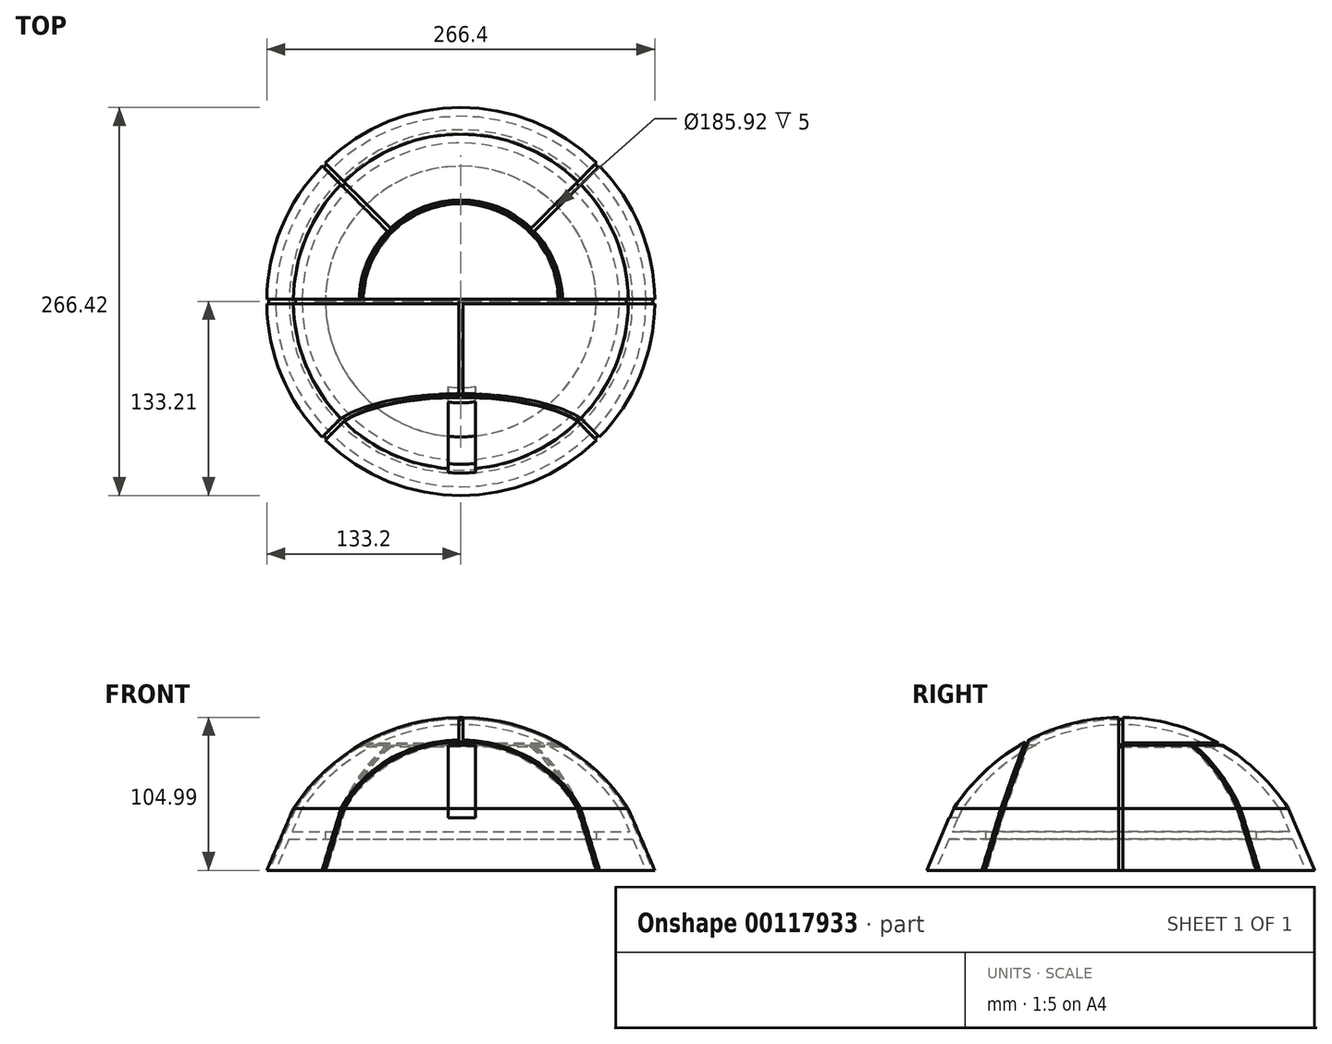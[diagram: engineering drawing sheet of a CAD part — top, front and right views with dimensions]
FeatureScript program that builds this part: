
annotation { "Feature Type Name" : "Feature", "Feature Type Description" : "" }
export const myFeature = defineFeature(function(context is Context, id is Id, definition is map)
    precondition{}
    {
        {
            var Q0;
            Q0=qCreatedBy(makeId("Front.planeOp"),FACE);
            var sketch = newSketch(context, id + "F0", { "sketchPlane" : qUnion([Q0])});
            skArc(sketch, "E0", {"start": v(114.97, 74.5) * mm, "mid": v(0, 137) * mm, "end": v(-114.97, 74.5) * mm});
            skLineSegment(sketch, "E1", {"start": v(-137, 0) * mm, "end": v(137, 0) * mm});
            skLineSegment(sketch, "E2", {"start": v(-133.21, 32) * mm, "end": v(133.21, 32) * mm});
            skLineSegment(sketch, "E3", {"start": v(-114.97, 74.5) * mm, "end": v(114.97, 74.5) * mm});
            skLineSegment(sketch, "E4", {"start": v(-114.97, 74.5) * mm, "end": v(-133.21, 32) * mm});
            skLineSegment(sketch, "E5", {"start": v(114.97, 74.5) * mm, "end": v(133.21, 32) * mm});
            skLineSegment(sketch, "E6", {"start": v(0, 137) * mm, "end": v(-99.44, 137) * mm, "construction": true});
            skLineSegment(sketch, "E7", {"start": v(0, 0) * mm, "end": v(0, 137) * mm});
            skArc(sketch, "E8", {"start": v(128.06, 32) * mm, "mid": v(0, 132) * mm, "end": v(-128.06, 32) * mm});
            skLineSegment(sketch, "E9", {"start": v(-108.97, 74.5) * mm, "end": v(-127.2, 32) * mm});
            skLineSegment(sketch, "E10", {"start": v(-115.81, 58.54) * mm, "end": v(-92.96, 58.54) * mm});
            skLineSegment(sketch, "E11", {"start": v(-92.96, 58.54) * mm, "end": v(-92.96, 53.54) * mm});
            skLineSegment(sketch, "E12", {"start": v(-92.96, 53.54) * mm, "end": v(-117.96, 53.54) * mm});
            skLineSegment(sketch, "E13", {"start": v(108.97, 74.5) * mm, "end": v(128.06, 32) * mm});
            skSolve(sketch);
        }
        {
            var Q0;
            {var subQ0=sQuery(id+"F0.wireOp",EDGE,"E4");Q0=makeQuery(id+"F0.imprint","IMPRINT",FACE,{"disambiguationData":[TD([[makeQuery(id+"F0.imprint","IMPRINT",EDGE,{"derivedFrom":subQ0}),1.0]])]});}
            var Q1;
            {var subQ0=sQuery(id+"F0.wireOp",EDGE,"E9");var subQ5=sQuery(id+"F0.wireOp",EDGE,"E2");var subQ7=makeQuery(id+"F0.imprint","INTERSECT",VERTEX,{"derivedFrom":[subQ5,subQ0]});Q1=makeQuery(id+"F0.imprint","IMPRINT",FACE,{"disambiguationData":[TD([[makeQuery(id+"F0.imprint","IMPRINT",EDGE,{"disambiguationData":[TD([[subQ7,1.0]])],"derivedFrom":subQ5}),1.0]])]});}
            var Q2;
            {var subQ0=sQuery(id+"F0.wireOp",EDGE,"E10");Q2=makeQuery(id+"F0.imprint","IMPRINT",FACE,{"disambiguationData":[TD([[makeQuery(id+"F0.imprint","IMPRINT",EDGE,{"derivedFrom":subQ0}),-1.0]])]});}
            var Q3;
            {var subQ1=sQuery(id+"F0.wireOp",EDGE,"E0");var subQ3=sQuery(id+"F0.wireOp",EDGE,"E7");var subQ4=makeQuery(id+"F0.imprint","INTERSECT",VERTEX,{"derivedFrom":[subQ1,subQ3]});Q3=makeQuery(id+"F0.imprint","IMPRINT",FACE,{"disambiguationData":[TD([[makeQuery(id+"F0.imprint","IMPRINT",EDGE,{"disambiguationData":[TD([[subQ4,1.0]])],"derivedFrom":subQ3}),1.0]])]});}
            var Q4;
            Q4=sQuery(id+"F0.wireOp",EDGE,"E7");
            revolve(context, id + "F1", {"entities" : qUnion([Q0, Q1, Q2, Q3]), "axis" : qUnion([Q4]), "revolveType" : RevolveType.FULL});
        }
        {
            var Q0;
            Q0=qCreatedBy(makeId("Top.planeOp"),FACE);
            cPlane(context, id + "F2", {"entities" : qUnion([Q0]), "cplaneType" : CPlaneType.OFFSET, "offset" : 74.5 * mm, "width" : 150 * mm, "height" : 150 * mm});
        }
        {
            var Q0;
            Q0=qCreatedBy(id+"F2.planeOp",FACE);
            var sketch = newSketch(context, id + "F3", { "sketchPlane" : qUnion([Q0])});
            skLineSegment(sketch, "E14", {"start": v(0, 0) * mm, "end": v(-58.68, 0) * mm, "construction": true});
            skLineSegment(sketch, "E15.bottom", {"start": v(-113.47, 1.5) * mm, "end": v(-116.47, 1.5) * mm});
            skLineSegment(sketch, "E15.top", {"start": v(-113.47, -1.5) * mm, "end": v(-116.47, -1.5) * mm});
            skLineSegment(sketch, "E15.left", {"start": v(-113.47, 1.5) * mm, "end": v(-113.47, -1.5) * mm});
            skLineSegment(sketch, "E15.right", {"start": v(-116.47, 1.5) * mm, "end": v(-116.47, -1.5) * mm});
            skPoint(sketch, "E15.middle", {"position": v(-114.97, 0) * mm});
            skLineSegment(sketch, "E16.1.0", {"start": v(-81.3, -79.18) * mm, "end": v(-83.42, -81.3) * mm});
            skLineSegment(sketch, "E16.1.1", {"start": v(-81.3, -79.18) * mm, "end": v(-79.18, -81.3) * mm});
            skLineSegment(sketch, "E16.1.2", {"start": v(-79.18, -81.3) * mm, "end": v(-81.3, -83.42) * mm});
            skLineSegment(sketch, "E16.1.3", {"start": v(-83.42, -81.3) * mm, "end": v(-81.3, -83.42) * mm});
            skLineSegment(sketch, "E16.2.0", {"start": v(-1.5, -113.47) * mm, "end": v(-1.5, -116.47) * mm});
            skLineSegment(sketch, "E16.2.1", {"start": v(-1.5, -113.47) * mm, "end": v(1.5, -113.47) * mm});
            skLineSegment(sketch, "E16.2.2", {"start": v(1.5, -113.47) * mm, "end": v(1.5, -116.47) * mm});
            skLineSegment(sketch, "E16.2.3", {"start": v(-1.5, -116.47) * mm, "end": v(1.5, -116.47) * mm});
            skLineSegment(sketch, "E16.3.0", {"start": v(79.18, -81.3) * mm, "end": v(81.3, -83.42) * mm});
            skLineSegment(sketch, "E16.3.1", {"start": v(79.18, -81.3) * mm, "end": v(81.3, -79.18) * mm});
            skLineSegment(sketch, "E16.3.2", {"start": v(81.3, -79.18) * mm, "end": v(83.42, -81.3) * mm});
            skLineSegment(sketch, "E16.3.3", {"start": v(81.3, -83.42) * mm, "end": v(83.42, -81.3) * mm});
            skLineSegment(sketch, "E16.4.0", {"start": v(113.47, -1.5) * mm, "end": v(116.47, -1.5) * mm});
            skLineSegment(sketch, "E16.4.1", {"start": v(113.47, -1.5) * mm, "end": v(113.47, 1.5) * mm});
            skLineSegment(sketch, "E16.4.2", {"start": v(113.47, 1.5) * mm, "end": v(116.47, 1.5) * mm});
            skLineSegment(sketch, "E16.4.3", {"start": v(116.47, -1.5) * mm, "end": v(116.47, 1.5) * mm});
            skLineSegment(sketch, "E16.5.0", {"start": v(81.3, 79.18) * mm, "end": v(83.42, 81.3) * mm});
            skLineSegment(sketch, "E16.5.1", {"start": v(81.3, 79.18) * mm, "end": v(79.18, 81.3) * mm});
            skLineSegment(sketch, "E16.5.2", {"start": v(79.18, 81.3) * mm, "end": v(81.3, 83.42) * mm});
            skLineSegment(sketch, "E16.5.3", {"start": v(83.42, 81.3) * mm, "end": v(81.3, 83.42) * mm});
            skLineSegment(sketch, "E16.6.0", {"start": v(1.5, 113.47) * mm, "end": v(1.5, 116.47) * mm});
            skLineSegment(sketch, "E16.6.1", {"start": v(1.5, 113.47) * mm, "end": v(-1.5, 113.47) * mm});
            skLineSegment(sketch, "E16.6.2", {"start": v(-1.5, 113.47) * mm, "end": v(-1.5, 116.47) * mm});
            skLineSegment(sketch, "E16.6.3", {"start": v(1.5, 116.47) * mm, "end": v(-1.5, 116.47) * mm});
            skLineSegment(sketch, "E16.7.0", {"start": v(-79.18, 81.3) * mm, "end": v(-81.3, 83.42) * mm});
            skLineSegment(sketch, "E16.7.1", {"start": v(-79.18, 81.3) * mm, "end": v(-81.3, 79.18) * mm});
            skLineSegment(sketch, "E16.7.2", {"start": v(-81.3, 79.18) * mm, "end": v(-83.42, 81.3) * mm});
            skLineSegment(sketch, "E16.7.3", {"start": v(-81.3, 83.42) * mm, "end": v(-83.42, 81.3) * mm});
            skPoint(sketch, "E16.center", {"position": v(0, 0) * mm});
            skLineSegment(sketch, "E17", {"start": v(81.3, -81.3) * mm, "end": v(-81.3, 81.3) * mm, "construction": true});
            skLineSegment(sketch, "E18", {"start": v(81.3, 81.3) * mm, "end": v(-81.3, -81.3) * mm, "construction": true});
            skLineSegment(sketch, "E19", {"start": v(-81.3, -81.3) * mm, "end": v(81.3, -81.3) * mm, "construction": true});
            skSolve(sketch);
        }
        {
            var Q0;
            Q0=makeQuery(id+"F3.imprint","IMPRINT",FACE,{"disambiguationData":[TD([[makeQuery(id+"F3.imprint","IMPRINT",EDGE,{"derivedFrom":sQuery(id+"F3.wireOp",EDGE,"E15.bottom")}),1.0]])]});
            var Q1;
            Q1=sQuery(id+"F0.wireOp",EDGE,"E4");
            sweep(context, id + "F4", {"operationType" : NewBodyOperationType.REMOVE, "profiles" : qUnion([Q0]), "path" : qUnion([Q1])});
        }
        {
            var Q0;
            Q0=makeQuery(id+"F3.imprint","IMPRINT",FACE,{"disambiguationData":[TD([[makeQuery(id+"F3.imprint","IMPRINT",EDGE,{"derivedFrom":sQuery(id+"F3.wireOp",EDGE,"E15.bottom")}),1.0]])]});
            var Q1;
            Q1=sQuery(id+"F0.wireOp",EDGE,"E0");
            sweep(context, id + "F5", {"operationType" : NewBodyOperationType.REMOVE, "profiles" : qUnion([Q0]), "path" : qUnion([Q1])});
        }
        {
            var Q0;
            Q0=makeQuery(id+"F3.imprint","IMPRINT",FACE,{"disambiguationData":[TD([[makeQuery(id+"F3.imprint","IMPRINT",EDGE,{"derivedFrom":sQuery(id+"F3.wireOp",EDGE,"E16.4.0")}),1.0]])]});
            var Q1;
            Q1=sQuery(id+"F0.wireOp",EDGE,"E5");
            sweep(context, id + "F6", {"operationType" : NewBodyOperationType.REMOVE, "profiles" : qUnion([Q0]), "path" : qUnion([Q1])});
        }
        {
            var Q0;
            Q0=qCreatedBy(makeId("Right.planeOp"),FACE);
            var sketch = newSketch(context, id + "F7", { "sketchPlane" : qUnion([Q0])});
            skArc(sketch, "E20", {"start": v(0, 137) * mm, "mid": v(-33.14, 132.93) * mm, "end": v(-64.32, 120.96) * mm});
            skLineSegment(sketch, "E21", {"start": v(0, 0) * mm, "end": v(-64.32, 120.96) * mm, "construction": true});
            skLineSegment(sketch, "E22", {"start": v(0, 137) * mm, "end": v(0, 0) * mm, "construction": true});
            skSolve(sketch);
        }
        {
            var Q0;
            Q0=qCreatedBy(makeId("Front.planeOp"),FACE);
            var sketch = newSketch(context, id + "F8", { "sketchPlane" : qUnion([Q0])});
            skLineSegment(sketch, "E23.bottom", {"start": v(1.5, 138.5) * mm, "end": v(-1.5, 138.5) * mm});
            skLineSegment(sketch, "E23.top", {"start": v(1.5, 135.5) * mm, "end": v(-1.5, 135.5) * mm});
            skLineSegment(sketch, "E23.left", {"start": v(1.5, 138.5) * mm, "end": v(1.5, 135.5) * mm});
            skLineSegment(sketch, "E23.right", {"start": v(-1.5, 138.5) * mm, "end": v(-1.5, 135.5) * mm});
            skPoint(sketch, "E23.middle", {"position": v(0, 137) * mm});
            skSolve(sketch);
        }
        {
            var Q0;
            Q0=makeQuery(id+"F8.imprint","IMPRINT",FACE,{"disambiguationData":[TD([[makeQuery(id+"F8.imprint","IMPRINT",EDGE,{"derivedFrom":sQuery(id+"F8.wireOp",EDGE,"E23.bottom")}),1.0]])]});
            var Q1;
            Q1=sQuery(id+"F7.wireOp",EDGE,"E20");
            sweep(context, id + "F9", {"operationType" : NewBodyOperationType.REMOVE, "profiles" : qUnion([Q0]), "path" : qUnion([Q1])});
        }
        {
            var Q0;
            Q0=qCreatedBy(makeId("Front.planeOp"),FACE);
            var sketch = newSketch(context, id + "F10", { "sketchPlane" : qUnion([Q0])});
            skCircle(sketch, "E24", {"center": v(0, 0) * mm, "radius": 137 * mm, "construction": true});
            skLineSegment(sketch, "E25", {"start": v(0, 0) * mm, "end": v(68.5, 118.65) * mm, "construction": true});
            skLineSegment(sketch, "E26", {"start": v(68.5, 118.65) * mm, "end": v(-68.5, 118.65) * mm});
            skLineSegment(sketch, "E27", {"start": v(-68.5, 118.65) * mm, "end": v(0, 0) * mm, "construction": true});
            skCircle(sketch, "E28", {"center": v(68.5, 118.65) * mm, "radius": 1.5 * mm});
            skLineSegment(sketch, "E29", {"start": v(67.75, 117.35) * mm, "end": v(69.05, 116.6) * mm});
            skLineSegment(sketch, "E30", {"start": v(69.05, 116.6) * mm, "end": v(70.55, 119.2) * mm});
            skLineSegment(sketch, "E31", {"start": v(67.75, 117.35) * mm, "end": v(66.45, 118.1) * mm});
            skLineSegment(sketch, "E32", {"start": v(70.55, 119.2) * mm, "end": v(67.95, 120.7) * mm});
            skLineSegment(sketch, "E33", {"start": v(67.95, 120.7) * mm, "end": v(66.45, 118.1) * mm});
            skSolve(sketch);
        }
        {
            var Q0;
            Q0=sQuery(id+"F10.wireOp",EDGE,"E26");
            cPlane(context, id + "F11", {"entities" : qUnion([Q0]), "cplaneType" : CPlaneType.LINE_ANGLE, "offset" : 25 * mm, "angle" : 90 * degree, "width" : 150 * mm, "height" : 150 * mm});
        }
        {
            var Q0;
            Q0=qCreatedBy(id+"F11.planeOp",FACE);
            var sketch = newSketch(context, id + "F12", { "sketchPlane" : qUnion([Q0])});
            skArc(sketch, "E34", {"start": v(68.5, 0) * mm, "mid": v(0, 68.5) * mm, "end": v(-68.5, 0) * mm});
            skLineSegment(sketch, "E35", {"start": v(-68.5, 0) * mm, "end": v(68.5, 0) * mm});
            skSolve(sketch);
        }
        {
            var Q0;
            {var subQ0=sQuery(id+"F10.wireOp",EDGE,"E28");var subQ3=makeQuery(id+"F10.imprint","INTERSECT",VERTEX,{"derivedFrom":[subQ0,sQuery(id+"F10.wireOp",EDGE,"E33")]});Q0=makeQuery(id+"F10.imprint","IMPRINT",FACE,{"disambiguationData":[TD([[makeQuery(id+"F10.imprint","IMPRINT",EDGE,{"disambiguationData":[TD([[subQ3,1.0]])],"derivedFrom":subQ0}),1.0]])]});}
            var Q1;
            {var subQ5=sQuery(id+"F10.wireOp",EDGE,"E31");Q1=makeQuery(id+"F10.imprint","IMPRINT",FACE,{"disambiguationData":[TD([[makeQuery(id+"F10.imprint","IMPRINT",EDGE,{"derivedFrom":subQ5}),-1.0]])]});}
            var Q2;
            {var subQ0=sQuery(id+"F10.wireOp",EDGE,"E33");var subQ1=sQuery(id+"F10.wireOp",EDGE,"E26");var subQ2=makeQuery(id+"F10.imprint","INTERSECT",VERTEX,{"derivedFrom":[subQ1,subQ0]});Q2=makeQuery(id+"F10.imprint","IMPRINT",FACE,{"disambiguationData":[TD([[makeQuery(id+"F10.imprint","IMPRINT",EDGE,{"disambiguationData":[TD([[subQ2,1.0]])],"derivedFrom":subQ1}),-1.0]])]});}
            var Q3;
            {var subQ0=sQuery(id+"F10.wireOp",EDGE,"E33");var subQ1=sQuery(id+"F10.wireOp",EDGE,"E28");var subQ2=makeQuery(id+"F10.imprint","INTERSECT",VERTEX,{"derivedFrom":[subQ1,subQ0]});Q3=makeQuery(id+"F10.imprint","IMPRINT",FACE,{"disambiguationData":[TD([[makeQuery(id+"F10.imprint","IMPRINT",EDGE,{"disambiguationData":[TD([[subQ2,1.0]])],"derivedFrom":subQ1}),-1.0]])]});}
            var Q4;
            {var subQ0=sQuery(id+"F10.wireOp",EDGE,"E32");var subQ1=sQuery(id+"F10.wireOp",EDGE,"E28");var subQ2=makeQuery(id+"F10.imprint","INTERSECT",VERTEX,{"derivedFrom":[subQ1,subQ0]});Q4=makeQuery(id+"F10.imprint","IMPRINT",FACE,{"disambiguationData":[TD([[makeQuery(id+"F10.imprint","IMPRINT",EDGE,{"disambiguationData":[TD([[subQ2,1.0]])],"derivedFrom":subQ1}),-1.0]])]});}
            var Q5;
            {var subQ0=sQuery(id+"F10.wireOp",EDGE,"E29");Q5=makeQuery(id+"F10.imprint","IMPRINT",FACE,{"disambiguationData":[TD([[makeQuery(id+"F10.imprint","IMPRINT",EDGE,{"derivedFrom":subQ0}),1.0]])]});}
            var Q6;
            Q6=sQuery(id+"F12.wireOp",EDGE,"E34");
            sweep(context, id + "F13", {"operationType" : NewBodyOperationType.REMOVE, "profiles" : qUnion([Q0, Q1, Q2, Q3, Q4, Q5]), "path" : qUnion([Q6])});
        }
        {
            var Q0;
            Q0=sQuery(id+"F3.wireOp",EDGE,"E18");
            cPlane(context, id + "F14", {"entities" : qUnion([Q0]), "cplaneType" : CPlaneType.LINE_ANGLE, "offset" : 25 * mm, "angle" : 90 * degree, "width" : 150 * mm, "height" : 150 * mm});
        }
        {
            var Q0;
            Q0=qCreatedBy(id+"F14.planeOp",FACE);
            var sketch = newSketch(context, id + "F15", { "sketchPlane" : qUnion([Q0])});
            skLineSegment(sketch, "E36", {"start": v(202.35, 74.5) * mm, "end": v(-236.58, 74.5) * mm, "construction": true});
            skLineSegment(sketch, "E37", {"start": v(177.5, 32) * mm, "end": v(-236.58, 32) * mm, "construction": true});
            skLineSegment(sketch, "E38", {"start": v(114.93, 74.5) * mm, "end": v(133.21, 32) * mm});
            skLineSegment(sketch, "E39", {"start": v(69.47, 117.89) * mm, "end": v(69.47, 32) * mm});
            skLineSegment(sketch, "E40", {"start": v(69.47, 32) * mm, "end": v(133.21, 32) * mm});
            skArc(sketch, "E41.trimOffspring", {"start": v(115.04, 74.26) * mm, "mid": v(94.8, 98.73) * mm, "end": v(69.47, 117.89) * mm});
            skSolve(sketch);
        }
        {
            var Q0;
            Q0=makeQuery(id+"F3.imprint","IMPRINT",FACE,{"disambiguationData":[TD([[makeQuery(id+"F3.imprint","IMPRINT",EDGE,{"derivedFrom":sQuery(id+"F3.wireOp",EDGE,"E16.5.0")}),1.0]])]});
            var Q1;
            Q1=sQuery(id+"F15.wireOp",EDGE,"E38");
            sweep(context, id + "F16", {"operationType" : NewBodyOperationType.REMOVE, "profiles" : qUnion([Q0]), "path" : qUnion([Q1])});
        }
        {
            var Q0;
            Q0=makeQuery(id+"F3.imprint","IMPRINT",FACE,{"disambiguationData":[TD([[makeQuery(id+"F3.imprint","IMPRINT",EDGE,{"derivedFrom":sQuery(id+"F3.wireOp",EDGE,"E16.5.0")}),1.0]])]});
            var Q1;
            Q1=sQuery(id+"F15.wireOp",EDGE,"E41.trimOffspring");
            sweep(context, id + "F17", {"operationType" : NewBodyOperationType.REMOVE, "profiles" : qUnion([Q0]), "path" : qUnion([Q1])});
        }
        {
            var Q0;
            Q0=sQuery(id+"F3.wireOp",EDGE,"E17");
            cPlane(context, id + "F18", {"entities" : qUnion([Q0]), "cplaneType" : CPlaneType.LINE_ANGLE, "offset" : 25 * mm, "angle" : 90 * degree, "width" : 150 * mm, "height" : 150 * mm});
        }
        {
            var Q0;
            Q0=qCreatedBy(id+"F18.planeOp",FACE);
            var sketch = newSketch(context, id + "F19", { "sketchPlane" : qUnion([Q0])});
            skArc(sketch, "E42", {"start": v(-114.97, 74.5) * mm, "mid": v(-125.9, 54.03) * mm, "end": v(-133.21, 32) * mm});
            skLineSegment(sketch, "E43", {"start": v(-154.96, 32) * mm, "end": v(196.04, 32) * mm, "construction": true});
            skLineSegment(sketch, "E44", {"start": v(-136.76, 74.5) * mm, "end": v(202.22, 74.5) * mm, "construction": true});
            skLineSegment(sketch, "E45", {"start": v(114.97, 74.5) * mm, "end": v(133.21, 32) * mm});
            skLineSegment(sketch, "E46", {"start": v(68.48, 118.66) * mm, "end": v(68.48, 32) * mm});
            skLineSegment(sketch, "E47", {"start": v(68.48, 32) * mm, "end": v(133.21, 32) * mm});
            skArc(sketch, "E48.trimOffspring", {"start": v(114.97, 74.5) * mm, "mid": v(94.35, 99.34) * mm, "end": v(68.48, 118.66) * mm});
            skSolve(sketch);
        }
        {
            var Q0;
            Q0=makeQuery(id+"F3.imprint","IMPRINT",FACE,{"disambiguationData":[TD([[makeQuery(id+"F3.imprint","IMPRINT",EDGE,{"derivedFrom":sQuery(id+"F3.wireOp",EDGE,"E16.7.0")}),1.0]])]});
            var Q1;
            Q1=sQuery(id+"F19.wireOp",EDGE,"E45");
            sweep(context, id + "F20", {"operationType" : NewBodyOperationType.REMOVE, "profiles" : qUnion([Q0]), "path" : qUnion([Q1])});
        }
        {
            var Q0;
            Q0=makeQuery(id+"F3.imprint","IMPRINT",FACE,{"disambiguationData":[TD([[makeQuery(id+"F3.imprint","IMPRINT",EDGE,{"derivedFrom":sQuery(id+"F3.wireOp",EDGE,"E16.7.0")}),1.0]])]});
            var Q1;
            Q1=sQuery(id+"F19.wireOp",EDGE,"E48.trimOffspring");
            sweep(context, id + "F21", {"operationType" : NewBodyOperationType.REMOVE, "profiles" : qUnion([Q0]), "path" : qUnion([Q1])});
        }
        {
            var Q0;
            Q0=sQuery(id+"F15.wireOp",EDGE,"E37");
            cPlane(context, id + "F22", {"entities" : qUnion([Q0]), "cplaneType" : CPlaneType.LINE_ANGLE, "offset" : 25 * mm, "angle" : 90 * degree, "width" : 150 * mm, "height" : 150 * mm});
        }
        {
            var Q0;
            Q0=qCreatedBy(id+"F22.planeOp",FACE);
            var sketch = newSketch(context, id + "F23", { "sketchPlane" : qUnion([Q0])});
            skArc(sketch, "E49", {"start": v(-133.21, 32) * mm, "mid": v(125.9, -54.03) * mm, "end": v(-114.97, 74.5) * mm});
            skLineSegment(sketch, "E50", {"start": v(-186.25, 32) * mm, "end": v(184.2, 32) * mm, "construction": true});
            skLineSegment(sketch, "E51", {"start": v(-158.48, 74.5) * mm, "end": v(175.2, 74.5) * mm, "construction": true});
            skLineSegment(sketch, "E52", {"start": v(-114.97, 74.5) * mm, "end": v(-133.21, 32) * mm});
            skSolve(sketch);
        }
        {
            var Q0;
            Q0=makeQuery(id+"F3.imprint","IMPRINT",FACE,{"disambiguationData":[TD([[makeQuery(id+"F3.imprint","IMPRINT",EDGE,{"derivedFrom":sQuery(id+"F3.wireOp",EDGE,"E16.1.0")}),1.0]])]});
            var Q1;
            Q1=sQuery(id+"F23.wireOp",EDGE,"E52");
            sweep(context, id + "F24", {"operationType" : NewBodyOperationType.REMOVE, "profiles" : qUnion([Q0]), "path" : qUnion([Q1])});
        }
        {
            var Q0;
            Q0=sQuery(id+"F19.wireOp",EDGE,"E43");
            cPlane(context, id + "F25", {"entities" : qUnion([Q0]), "cplaneType" : CPlaneType.LINE_ANGLE, "offset" : 25 * mm, "angle" : 90 * degree, "width" : 150 * mm, "height" : 150 * mm});
        }
        {
            var Q0;
            Q0=qCreatedBy(id+"F25.planeOp",FACE);
            var sketch = newSketch(context, id + "F26", { "sketchPlane" : qUnion([Q0])});
            skArc(sketch, "E53", {"start": v(-133.21, 32) * mm, "mid": v(125.9, -54.03) * mm, "end": v(-114.97, 74.5) * mm});
            skLineSegment(sketch, "E54", {"start": v(-151.8, 74.5) * mm, "end": v(39.62, 74.5) * mm, "construction": true});
            skLineSegment(sketch, "E55", {"start": v(-155.93, 32) * mm, "end": v(41.16, 32) * mm, "construction": true});
            skLineSegment(sketch, "E56", {"start": v(-114.97, 74.5) * mm, "end": v(-133.21, 32) * mm});
            skSolve(sketch);
        }
        {
            var Q0;
            Q0=makeQuery(id+"F3.imprint","IMPRINT",FACE,{"disambiguationData":[TD([[makeQuery(id+"F3.imprint","IMPRINT",EDGE,{"derivedFrom":sQuery(id+"F3.wireOp",EDGE,"E16.3.0")}),1.0]])]});
            var Q1;
            Q1=sQuery(id+"F26.wireOp",EDGE,"E56");
            sweep(context, id + "F27", {"operationType" : NewBodyOperationType.REMOVE, "profiles" : qUnion([Q0]), "path" : qUnion([Q1])});
        }
        {
            var Q0;
            Q0=sQuery(id+"F3.wireOp",EDGE,"E19");
            cPlane(context, id + "F28", {"entities" : qUnion([Q0]), "cplaneType" : CPlaneType.LINE_ANGLE, "offset" : 25 * mm, "angle" : 340 * degree, "width" : 150 * mm, "height" : 150 * mm});
        }
        {
            var Q0;
            Q0=qCreatedBy(id+"F28.planeOp",FACE);
            var sketch = newSketch(context, id + "F29", { "sketchPlane" : qUnion([Q0])});
            skArc(sketch, "E57", {"start": v(81.3, 42.2) * mm, "mid": v(0, 91.25) * mm, "end": v(-81.3, 42.2) * mm});
            skSolve(sketch);
        }
        {
            var Q0;
            Q0=makeQuery(id+"F3.imprint","IMPRINT",FACE,{"disambiguationData":[TD([[makeQuery(id+"F3.imprint","IMPRINT",EDGE,{"derivedFrom":sQuery(id+"F3.wireOp",EDGE,"E16.1.0")}),1.0]])]});
            var Q1;
            Q1=sQuery(id+"F29.wireOp",EDGE,"E57");
            sweep(context, id + "F30", {"operationType" : NewBodyOperationType.REMOVE, "profiles" : qUnion([Q0]), "path" : qUnion([Q1])});
        }
        {
            var Q0;
            Q0=qCreatedBy(makeId("Front.planeOp"),FACE);
            cPlane(context, id + "F31", {"entities" : qUnion([Q0]), "cplaneType" : CPlaneType.OFFSET, "offset" : 150 * mm, "width" : 150 * mm, "height" : 150 * mm});
        }
        {
            var Q0;
            Q0=qCreatedBy(id+"F31.planeOp",FACE);
            var sketch = newSketch(context, id + "F32", { "sketchPlane" : qUnion([Q0])});
            skLineSegment(sketch, "E58", {"start": v(0, 0) * mm, "end": v(0, 142.08) * mm, "construction": true});
            skLineSegment(sketch, "E59.bottom", {"start": v(-8.62, 118) * mm, "end": v(10, 118) * mm});
            skLineSegment(sketch, "E59.top", {"start": v(-8.62, 68) * mm, "end": v(10, 68) * mm});
            skLineSegment(sketch, "E59.left", {"start": v(-8.62, 118) * mm, "end": v(-8.62, 68) * mm});
            skLineSegment(sketch, "E59.right", {"start": v(10, 118) * mm, "end": v(10, 68) * mm});
            skSolve(sketch);
        }
        {
            var Q0;
            Q0=makeQuery(id+"F32.imprint","IMPRINT",FACE,{"disambiguationData":[TD([[makeQuery(id+"F32.imprint","IMPRINT",EDGE,{"derivedFrom":sQuery(id+"F32.wireOp",EDGE,"E59.bottom")}),-1.0]])]});
            extrude(context, id + "F33", {"entities" : qUnion([Q0]), "operationType" : NewBodyOperationType.REMOVE, "oppositeDirection" : true, "depth" : 123.02 * mm});
        }
    });
